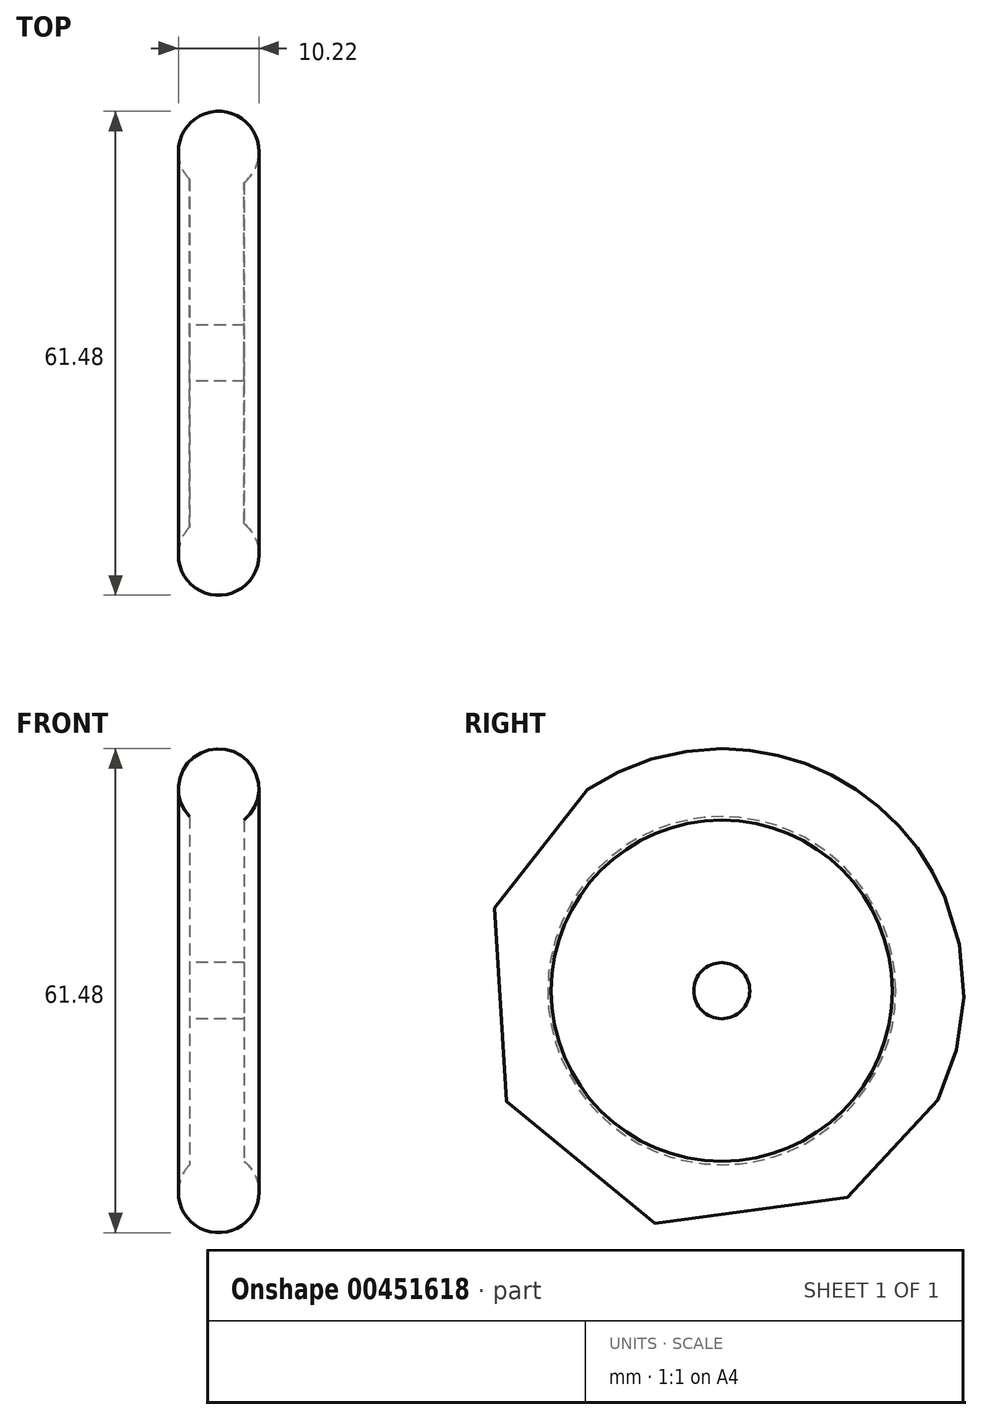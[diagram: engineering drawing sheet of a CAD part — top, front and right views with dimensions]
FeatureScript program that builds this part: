
annotation { "Feature Type Name" : "Feature", "Feature Type Description" : "" }
export const myFeature = defineFeature(function(context is Context, id is Id, definition is map)
    precondition{}
    {
        {
            var Q0;
            Q0=qCreatedBy(makeId("Front.planeOp"),FACE);
            var sketch = newSketch(context, id + "F0", { "sketchPlane" : qUnion([Q0])});
            skArc(sketch, "E0", {"start": v(3.23, 21.67) * mm, "mid": v(0.32, 30.73) * mm, "end": v(-3.7, 22.1) * mm});
            skLineSegment(sketch, "E1", {"start": v(-3.7, 22.1) * mm, "end": v(-3.7, 3.56) * mm});
            skLineSegment(sketch, "E2", {"start": v(3.23, 21.67) * mm, "end": v(3.23, 3.56) * mm});
            skLineSegment(sketch, "E3", {"start": v(3.23, 3.56) * mm, "end": v(-3.7, 3.56) * mm});
            skLineSegment(sketch, "E4", {"start": v(-6.85, 0) * mm, "end": v(8.9, 0) * mm});
            skSolve(sketch);
        }
        {
            var Q0;
            Q0=makeQuery(id+"F0.imprint","IMPRINT",FACE,{"disambiguationData":[TD([[makeQuery(id+"F0.imprint","IMPRINT",EDGE,{"derivedFrom":sQuery(id+"F0.wireOp",EDGE,"E0")}),1.0]])]});
            var Q1;
            Q1=sQuery(id+"F0.wireOp",EDGE,"E4");
            revolve(context, id + "F1", {"entities" : qUnion([Q0]), "axis" : qUnion([Q1]), "revolveType" : RevolveType.FULL});
        }
    });
